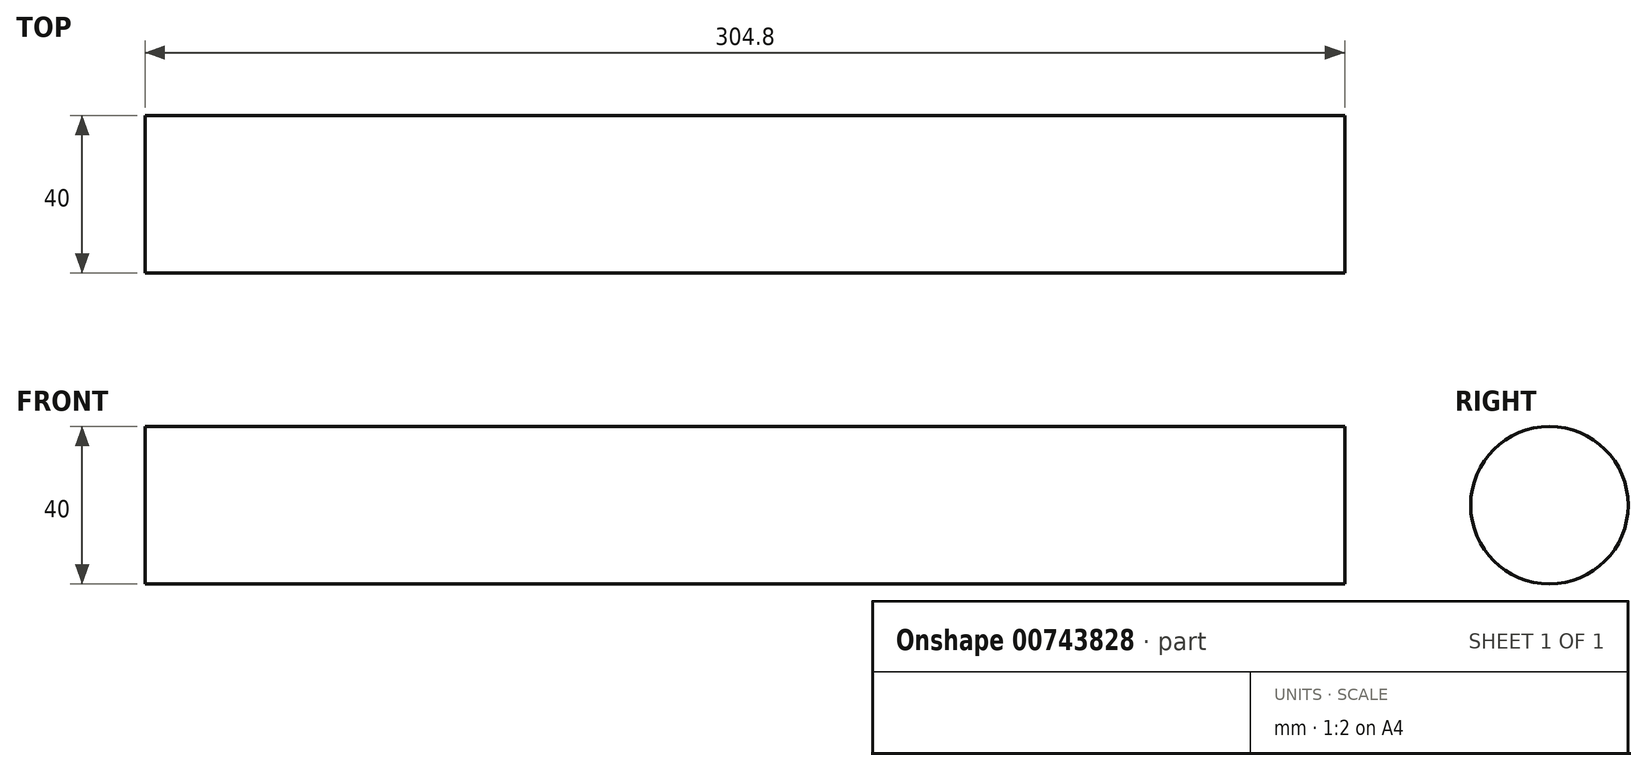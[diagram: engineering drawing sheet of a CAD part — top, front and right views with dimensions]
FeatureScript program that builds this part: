
annotation { "Feature Type Name" : "Feature", "Feature Type Description" : "" }
export const myFeature = defineFeature(function(context is Context, id is Id, definition is map)
    precondition{}
    {
        {
            var Q0;
            Q0=qCreatedBy(makeId("Right.planeOp"),FACE);
            var sketch = newSketch(context, id + "F0", { "sketchPlane" : qUnion([Q0])});
            skCircle(sketch, "E0", {"center": v(0, 0) * mm, "radius": 20 * mm});
            skSolve(sketch);
        }
        {
            var Q0;
            Q0=makeQuery(id+"F0.imprint","IMPRINT",FACE,{"disambiguationData":[TD([[makeQuery(id+"F0.imprint","IMPRINT",EDGE,{"derivedFrom":sQuery(id+"F0.wireOp",EDGE,"E0")}),1.0]])]});
            extrude(context, id + "F1", {"entities" : qUnion([Q0]), "endBound" : BoundingType.SYMMETRIC, "depth" : 304.8 * mm, "offsetDistance" : 25.4 * mm});
        }
    });
